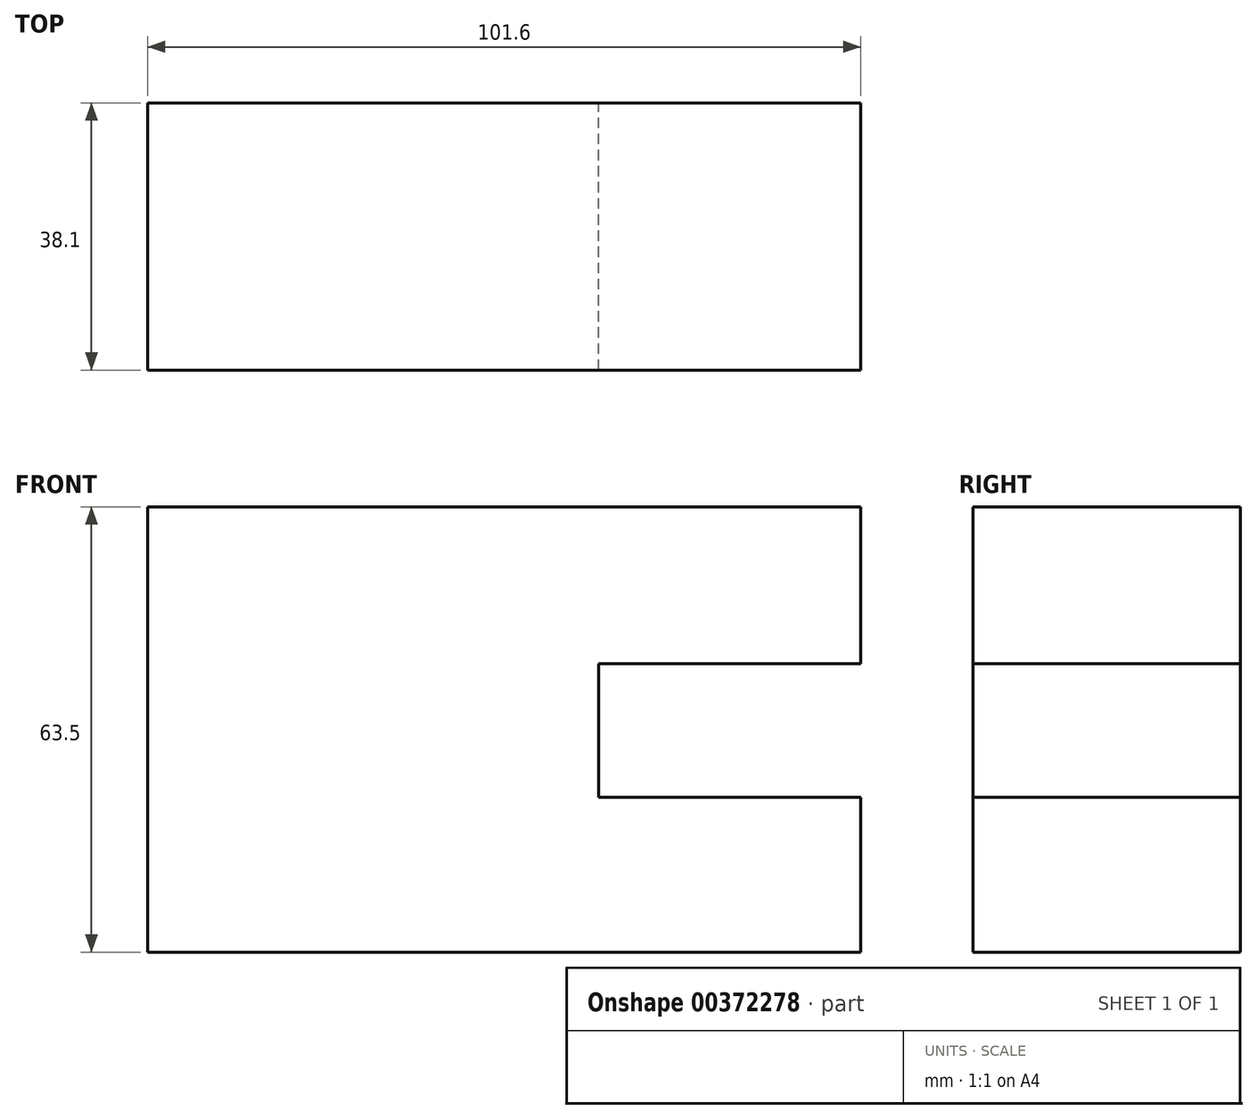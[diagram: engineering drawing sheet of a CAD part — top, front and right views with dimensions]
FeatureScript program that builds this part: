
annotation { "Feature Type Name" : "Feature", "Feature Type Description" : "" }
export const myFeature = defineFeature(function(context is Context, id is Id, definition is map)
    precondition{}
    {
        {
            var Q0;
            Q0=qCreatedBy(makeId("Front.planeOp"),FACE);
            var sketch = newSketch(context, id + "F0", { "sketchPlane" : qUnion([Q0])});
            skLineSegment(sketch, "E0.bottom", {"start": v(-50.8, 31.75) * mm, "end": v(50.8, 31.75) * mm});
            skLineSegment(sketch, "E0.top", {"start": v(-50.8, -31.75) * mm, "end": v(50.8, -31.75) * mm});
            skLineSegment(sketch, "E0.left", {"start": v(-50.8, 31.75) * mm, "end": v(-50.8, -31.75) * mm});
            skLineSegment(sketch, "E0.right", {"start": v(50.8, 31.75) * mm, "end": v(50.8, -31.75) * mm});
            skPoint(sketch, "E0.middle", {"position": v(0, 0) * mm});
            skSolve(sketch);
        }
        {
            var Q0;
            Q0 = qSketchRegion(id + "F0", true);
            extrude(context, id + "F1", {"entities" : qUnion([Q0]), "depth" : 38.1 * mm});
        }
        {
            var Q0;
            Q0=qCreatedBy(makeId("Front.planeOp"),FACE);
            var sketch = newSketch(context, id + "F2", { "sketchPlane" : qUnion([Q0])});
            skLineSegment(sketch, "E1.bottom", {"start": v(51.55, -9.67) * mm, "end": v(13.45, -9.67) * mm});
            skLineSegment(sketch, "E1.top", {"start": v(51.55, 9.38) * mm, "end": v(13.45, 9.38) * mm});
            skLineSegment(sketch, "E1.left", {"start": v(51.55, -9.67) * mm, "end": v(51.55, 9.38) * mm});
            skLineSegment(sketch, "E1.right", {"start": v(13.45, -9.67) * mm, "end": v(13.45, 9.38) * mm});
            skSolve(sketch);
        }
        {
            var Q0;
            Q0 = qSketchRegion(id + "F2", true);
            extrude(context, id + "F3", {"entities" : qUnion([Q0]), "operationType" : NewBodyOperationType.REMOVE, "oppositeDirection" : true, "depth" : -38.1 * mm});
        }
    });
